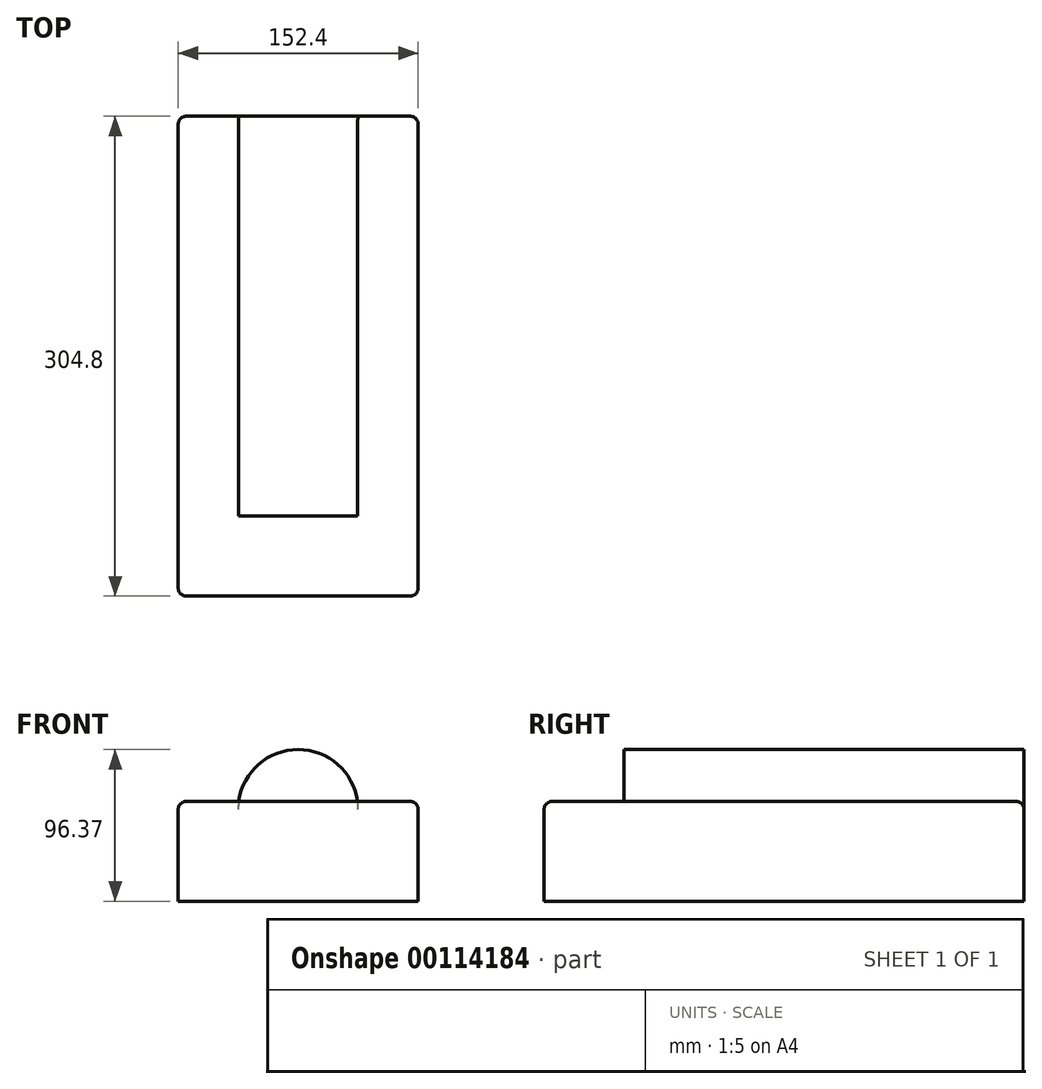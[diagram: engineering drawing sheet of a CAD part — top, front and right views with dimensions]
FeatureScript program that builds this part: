
annotation { "Feature Type Name" : "Feature", "Feature Type Description" : "" }
export const myFeature = defineFeature(function(context is Context, id is Id, definition is map)
    precondition{}
    {
        {
            var Q0;
            Q0=qCreatedBy(makeId("Front.planeOp"),FACE);
            var sketch = newSketch(context, id + "F0", { "sketchPlane" : qUnion([Q0])});
            skLineSegment(sketch, "E0.bottom", {"start": v(-76.2, 31.75) * mm, "end": v(76.2, 31.75) * mm});
            skLineSegment(sketch, "E0.top", {"start": v(-76.2, -31.75) * mm, "end": v(76.2, -31.75) * mm});
            skLineSegment(sketch, "E0.left", {"start": v(-76.2, 31.75) * mm, "end": v(-76.2, -31.75) * mm});
            skLineSegment(sketch, "E0.right", {"start": v(76.2, 31.75) * mm, "end": v(76.2, -31.75) * mm});
            skPoint(sketch, "E0.middle", {"position": v(0, 0) * mm});
            skSolve(sketch);
        }
        {
            var Q0;
            Q0=makeQuery(id+"F0.imprint","IMPRINT",FACE,{"disambiguationData":[TD([[makeQuery(id+"F0.imprint","IMPRINT",EDGE,{"derivedFrom":sQuery(id+"F0.wireOp",EDGE,"E0.bottom")}),-1.0]])]});
            extrude(context, id + "F1", {"entities" : qUnion([Q0]), "depth" : 304.8 * mm});
        }
        {
            var Q0;
            Q0=makeQuery(id+"F1.opExtrude","SWEPT_EDGE",EDGE,{"disambiguationData":[OSD([sQuery(id+"F0.wireOp",EDGE,"E0.bottom"),sQuery(id+"F0.wireOp",EDGE,"E0.right")])]});
            var Q1;
            Q1=makeQuery(id+"F1.opExtrude","CAP_EDGE",EDGE,{"disambiguationData":[OSD([sQuery(id+"F0.wireOp",EDGE,"E0.right")])],"isStart":false});
            var Q2;
            Q2=makeQuery(id+"F1.opExtrude","CAP_EDGE",EDGE,{"disambiguationData":[OSD([sQuery(id+"F0.wireOp",EDGE,"E0.right")])],"isStart":true});
            var Q3;
            Q3=makeQuery(id+"F1.opExtrude","CAP_EDGE",EDGE,{"disambiguationData":[OSD([sQuery(id+"F0.wireOp",EDGE,"E0.bottom")])],"isStart":true});
            var Q4;
            Q4=makeQuery(id+"F1.opExtrude","CAP_EDGE",EDGE,{"disambiguationData":[OSD([sQuery(id+"F0.wireOp",EDGE,"E0.left")])],"isStart":true});
            var Q5;
            Q5=makeQuery(id+"F1.opExtrude","SWEPT_EDGE",EDGE,{"disambiguationData":[OSD([sQuery(id+"F0.wireOp",EDGE,"E0.bottom"),sQuery(id+"F0.wireOp",EDGE,"E0.left")])]});
            var Q6;
            Q6=makeQuery(id+"F1.opExtrude","CAP_EDGE",EDGE,{"disambiguationData":[OSD([sQuery(id+"F0.wireOp",EDGE,"E0.left")])],"isStart":false});
            var Q7;
            Q7=makeQuery(id+"F1.opExtrude","CAP_EDGE",EDGE,{"disambiguationData":[OSD([sQuery(id+"F0.wireOp",EDGE,"E0.bottom")])],"isStart":false});
            fillet(context, id + "F2", {"entities" : qUnion([Q0, Q1, Q2, Q3, Q4, Q5, Q6, Q7]), "radius" : 5.08 * mm, "tangentPropagation" : true, "allowEdgeOverflow" : false});
        }
        {
            var Q0;
            Q0=qCreatedBy(makeId("Front.planeOp"),FACE);
            var sketch = newSketch(context, id + "F3", { "sketchPlane" : qUnion([Q0])});
            skCircle(sketch, "E1", {"center": v(0, 26.52) * mm, "radius": 38.1 * mm});
            skSolve(sketch);
        }
        {
            var Q0;
            Q0 = qSketchRegion(id + "F3", true);
            extrude(context, id + "F4", {"entities" : qUnion([Q0]), "operationType" : NewBodyOperationType.ADD, "depth" : 254 * mm});
        }
    });
